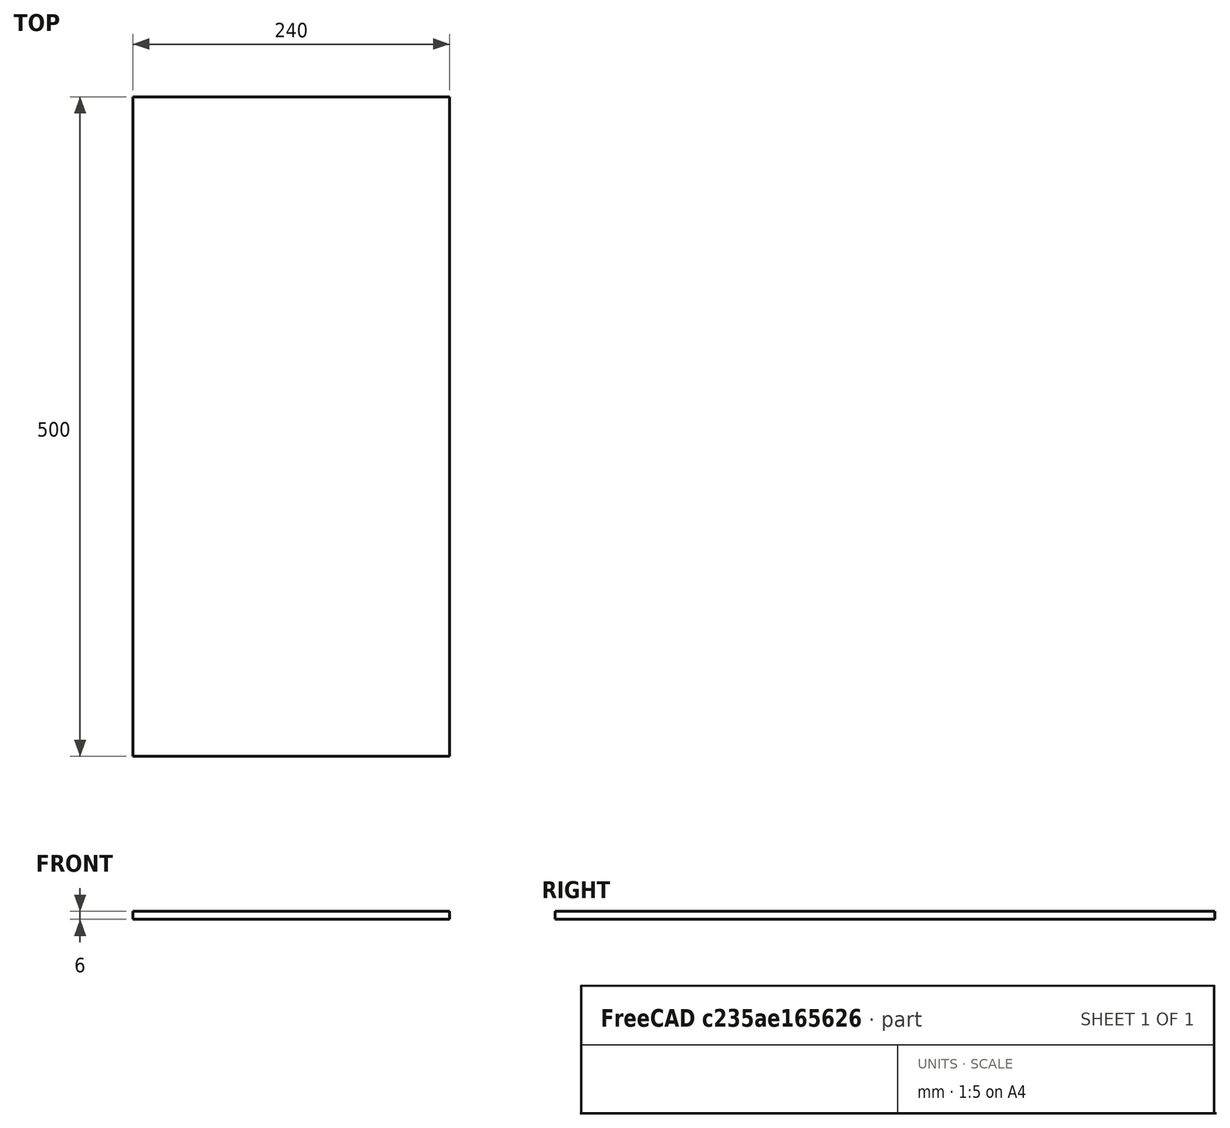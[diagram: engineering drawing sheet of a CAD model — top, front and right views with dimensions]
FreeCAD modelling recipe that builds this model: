
FCSTD DOCUMENT  (FreeCAD 0.18R4 (GitTag))
Label: Gabinete_Base
License: All rights reserved
LicenseURL: http://en.wikipedia.org/wiki/All_rights_reserved
objects: Sketcher::SketchObject×1, PartDesign::Pad×1, PartDesign::Body×1
note: 4 computed .brp shape members not serialized (recipe doc carries the construction recipe); baked Part::Feature solids carry a one-line shape summary decoded from their .brp

FEATURE [Sketcher::SketchObject] Sketch
  MapMode = 5
  Support = -> [XY_Plane]
  sketch-geometry (4):
    g0: LineSegment StartX=0 StartY=0 StartZ=0 EndX=240 EndY=0 EndZ=0
    g1: LineSegment StartX=240 StartY=0 StartZ=0 EndX=240 EndY=500 EndZ=0
    g2: LineSegment StartX=240 StartY=500 StartZ=0 EndX=0 EndY=500 EndZ=0
    g3: LineSegment StartX=0 StartY=500 StartZ=0 EndX=0 EndY=0 EndZ=0
  constraints (11):
    c: Coincident(g0,g1)
    c: Coincident(g1,g2)
    c: Coincident(g2,g3)
    c: Coincident(g3,g0)
    c: Horizontal(g0)
    c: Horizontal(g2)
    c: Vertical(g1)
    c: Vertical(g3)
    c: DistanceX(g0,g0) = 240
    c: DistanceY(g3,g3) = 500
    c: Coincident(g0,g-1)
FEATURE [PartDesign::Pad] Pad
  Length = 6
  Length2 = 100
  Profile = -> Sketch
  Type = 0
FEATURE [PartDesign::Body] Body
  Group = -> [Sketch,Pad]
  Origin = -> Origin
  Tip = -> Pad
